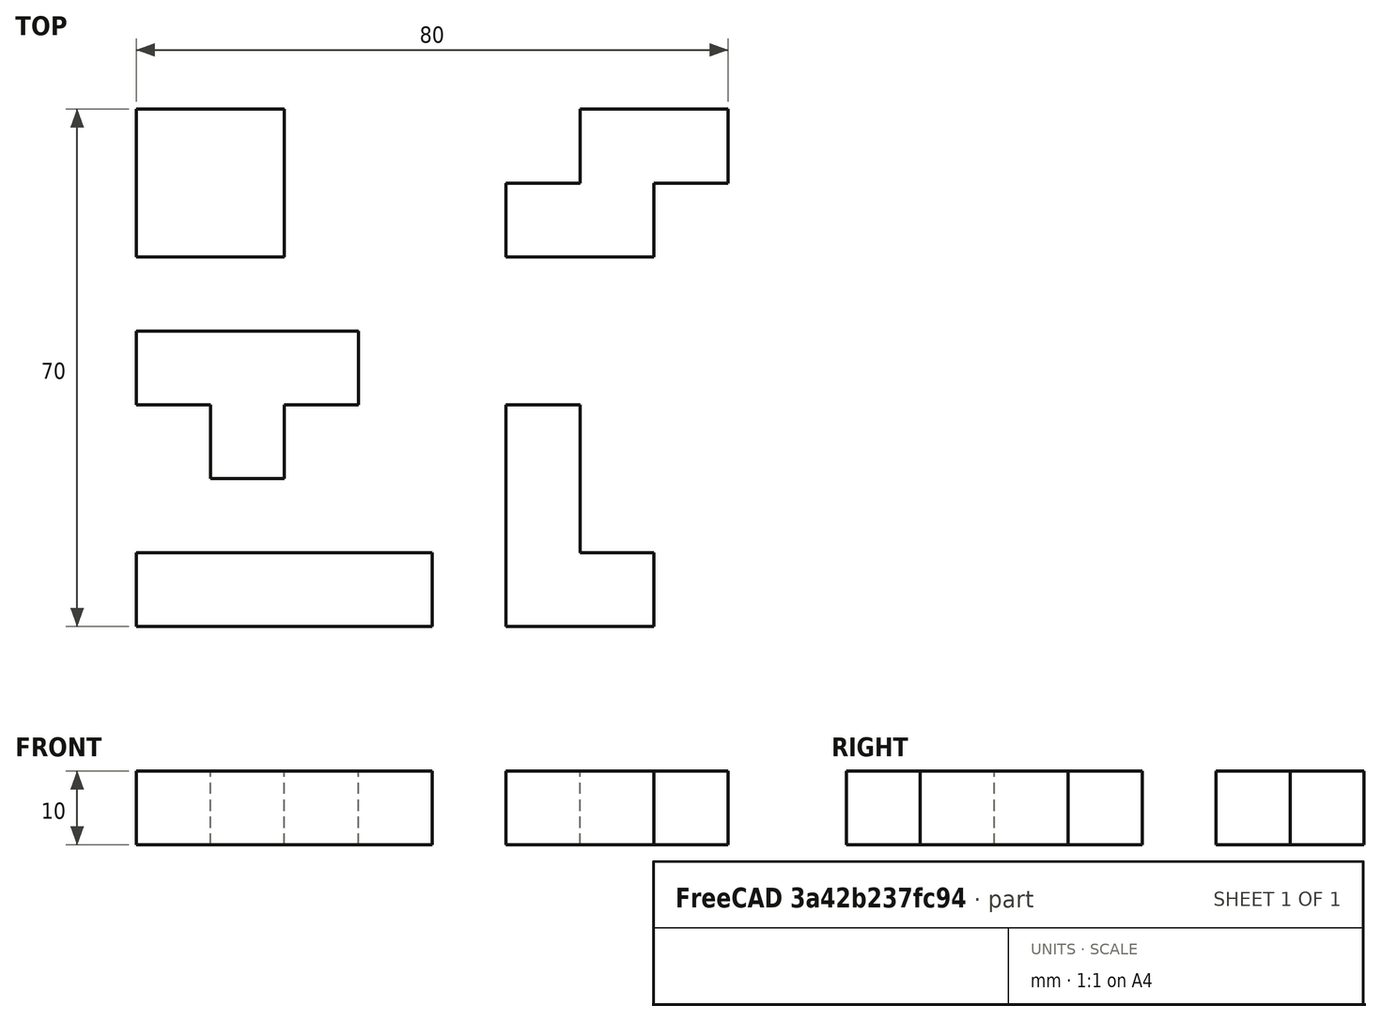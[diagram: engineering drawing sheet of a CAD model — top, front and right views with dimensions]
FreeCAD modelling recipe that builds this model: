
FCSTD DOCUMENT  (FreeCAD 0.21R33694 (Git))
Label: OJT1_T05RO3_unionstetris
License: All rights reserved
LicenseURL: https://en.wikipedia.org/wiki/All_rights_reserved
objects: Part::Box×9, Part::MultiFuse×4, Part::Refine×4
note: 17 computed .brp shape members not serialized (recipe doc carries the construction recipe); baked Part::Feature solids carry a one-line shape summary decoded from their .brp

FEATURE [Part::Box] Box  label="Figura 1"
  AttacherType = Attacher::AttachEngine3D
  Height = 10
  Length = 40
  Width = 10
FEATURE [Part::Box] Box001  label="Cub001"
  AttacherType = Attacher::AttachEngine3D
  Height = 10
  Length = 10
  Placement = pos=(10,20,0) rot=(-1,0,1;0rad)
  Width = 10
  expr: .Placement.Base.x = 10
  expr: .Placement.Base.y = 20
  expr: .Placement.Base.z = 0
FEATURE [Part::Box] Box002  label="Cub002"
  AttacherType = Attacher::AttachEngine3D
  Height = 10
  Length = 30
  Placement = pos=(0,30,0) rot=(0,0,1;0rad)
  Width = 10
  expr: .Placement.Base.x = 0 mm
  expr: .Placement.Base.y = 30
FEATURE [Part::MultiFuse] Fusion
  AttacherType = Attacher::AttachEngine3D
  Shapes = -> [Box002,Box001]
FEATURE [Part::Refine] Fusion001  label="Figura2"
  Source = -> Fusion
FEATURE [Part::Box] Box003  label="Cub"
  AttacherType = Attacher::AttachEngine3D
  Height = 10
  Length = 20
  Placement = pos=(50,0,0) rot=(0,0,1;0rad)
  Width = 10
  expr: .Placement.Base.x = 50
FEATURE [Part::Box] Box004  label="Cub003"
  AttacherType = Attacher::AttachEngine3D
  Height = 10
  Length = 10
  Placement = pos=(50,0,0) rot=(0,0,1;0rad)
  Width = 30
  expr: .Placement.Base.x = 50
FEATURE [Part::MultiFuse] Fusion002
  Shapes = -> [Box003,Box004]
FEATURE [Part::Refine] Fusion003  label="Figura3"
  Source = -> Fusion002
FEATURE [Part::Box] Box005  label="Cub004"
  AttacherType = Attacher::AttachEngine3D
  Height = 10
  Length = 20
  Placement = pos=(0,50,0) rot=(0,0,1;0rad)
  Width = 10
  expr: .Placement.Base.y = 50
FEATURE [Part::Box] Box006  label="Cub005"
  AttacherType = Attacher::AttachEngine3D
  Height = 10
  Length = 20
  Placement = pos=(0,60,0) rot=(0,0,1;0rad)
  Width = 10
  expr: .Placement.Base.y = 60
FEATURE [Part::MultiFuse] Fusion004
  Shapes = -> [Box005,Box006]
FEATURE [Part::Refine] Fusion005
  Source = -> Fusion004
  expr: .Placement.Base.x = 0
FEATURE [Part::Box] Box007  label="Cub006"
  AttacherType = Attacher::AttachEngine3D
  Height = 10
  Length = 20
  Placement = pos=(50,50,0) rot=(0,0,1;0rad)
  Width = 10
  expr: .Placement.Base.x = 50
  expr: .Placement.Base.y = 50
FEATURE [Part::Box] Box008  label="Cub007"
  AttacherType = Attacher::AttachEngine3D
  Height = 10
  Length = 20
  Placement = pos=(60,60,0) rot=(0,0,1;0rad)
  Width = 10
  expr: .Placement.Base.x = 60
  expr: .Placement.Base.y = 60
FEATURE [Part::MultiFuse] Fusion006
  Shapes = -> [Box007,Box008]
FEATURE [Part::Refine] Fusion007
  Source = -> Fusion006
  expr: .Placement.Base.x = -10
